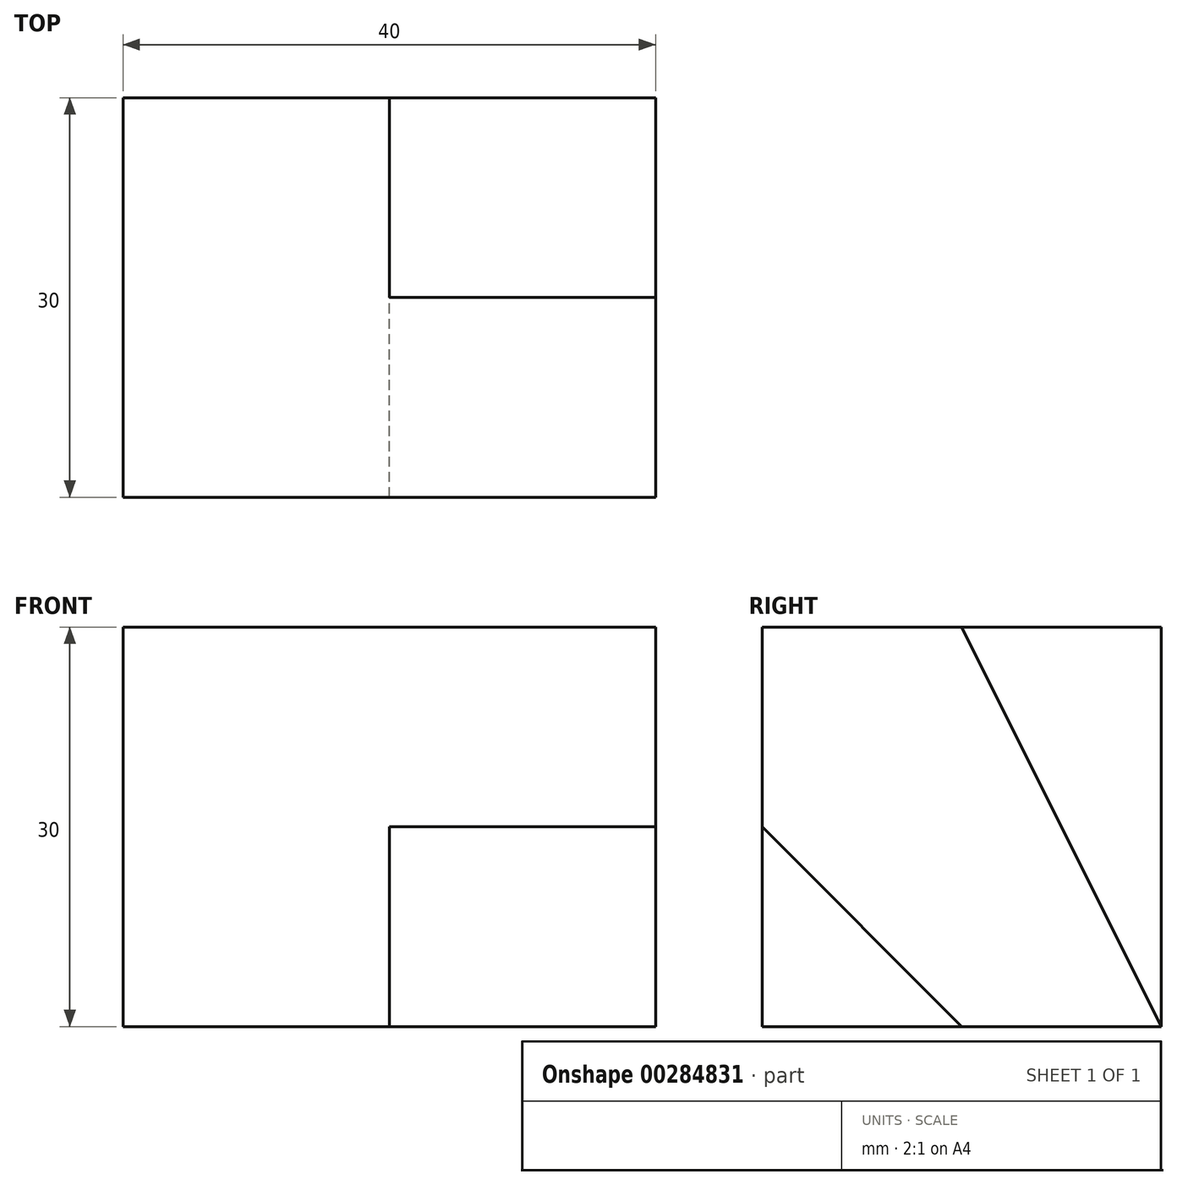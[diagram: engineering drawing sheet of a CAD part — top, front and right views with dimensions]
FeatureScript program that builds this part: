
annotation { "Feature Type Name" : "Feature", "Feature Type Description" : "" }
export const myFeature = defineFeature(function(context is Context, id is Id, definition is map)
    precondition{}
    {
        {
            var Q0;
            Q0=qCreatedBy(makeId("Right.planeOp"),FACE);
            var sketch = newSketch(context, id + "F0", { "sketchPlane" : qUnion([Q0])});
            skLineSegment(sketch, "E0.bottom", {"start": v(0, 0) * mm, "end": v(30, 0) * mm});
            skLineSegment(sketch, "E0.top", {"start": v(0, 30) * mm, "end": v(30, 30) * mm});
            skLineSegment(sketch, "E0.left", {"start": v(0, 0) * mm, "end": v(0, 30) * mm});
            skLineSegment(sketch, "E0.right", {"start": v(30, 0) * mm, "end": v(30, 30) * mm});
            skLineSegment(sketch, "E1", {"start": v(0, 15) * mm, "end": v(30, 15) * mm});
            skLineSegment(sketch, "E2", {"start": v(15, 30) * mm, "end": v(15, 0) * mm});
            skSolve(sketch);
        }
        {
            var Q0;
            Q0=qSketchRegion(id+"F0",true);
            extrude(context, id + "F1", {"entities" : qUnion([Q0]), "depth" : 20 * mm});
        }
        {
            var Q0;
            {var subQ0=sQuery(id+"F0.wireOp",EDGE,"E0.right");var subQ1=sQuery(id+"F0.wireOp",EDGE,"E0.bottom");var subQ2=makeQuery(id+"F0.imprint","INTERSECT",VERTEX,{"derivedFrom":[subQ1,subQ0]});Q0=makeQuery(id+"F0.imprint","IMPRINT",FACE,{"disambiguationData":[TD([[makeQuery(id+"F0.imprint","IMPRINT",EDGE,{"disambiguationData":[TD([[subQ2,1.0]])],"derivedFrom":subQ1}),1.0]])]});}
            var Q1;
            {var subQ0=sQuery(id+"F0.wireOp",EDGE,"E0.right");var subQ1=sQuery(id+"F0.wireOp",EDGE,"E0.top");var subQ2=makeQuery(id+"F0.imprint","INTERSECT",VERTEX,{"derivedFrom":[subQ1,subQ0]});Q1=makeQuery(id+"F0.imprint","IMPRINT",FACE,{"disambiguationData":[TD([[makeQuery(id+"F0.imprint","IMPRINT",EDGE,{"disambiguationData":[TD([[subQ2,1.0]])],"derivedFrom":subQ1}),-1.0]])]});}
            var Q2;
            {var subQ0=sQuery(id+"F0.wireOp",EDGE,"E0.left");var subQ1=sQuery(id+"F0.wireOp",EDGE,"E0.top");var subQ2=makeQuery(id+"F0.imprint","INTERSECT",VERTEX,{"derivedFrom":[subQ1,subQ0]});Q2=makeQuery(id+"F0.imprint","IMPRINT",FACE,{"disambiguationData":[TD([[makeQuery(id+"F0.imprint","IMPRINT",EDGE,{"disambiguationData":[TD([[subQ2,-1.0]])],"derivedFrom":subQ1}),-1.0]])]});}
            extrude(context, id + "F2", {"entities" : qUnion([Q0, Q1, Q2]), "operationType" : NewBodyOperationType.ADD, "depth" : 40 * mm});
        }
        {
            var Q0;
            Q0=makeQuery(id+"F2.opExtrude","CAP_FACE",FACE,{"disambiguationData":[OSD([sQuery(id+"F0.wireOp",EDGE,"E0.bottom"),sQuery(id+"F0.wireOp",EDGE,"E0.top"),sQuery(id+"F0.wireOp",EDGE,"E0.left"),sQuery(id+"F0.wireOp",EDGE,"E0.right"),sQuery(id+"F0.wireOp",EDGE,"E1"),sQuery(id+"F0.wireOp",EDGE,"E2")])],"isStart":false});
            var sketch = newSketch(context, id + "F3", { "sketchPlane" : qUnion([Q0])});
            skLineSegment(sketch, "E3", {"start": v(15, 30) * mm, "end": v(30, 0) * mm});
            skSolve(sketch);
        }
        {
            var Q0;
            Q0=qSketchRegion(id+"F3",true);
            var Q1;
            {var subQ0=sQuery(id+"F3.wireOp",EDGE,"E3");Q1=makeQuery(id+"F3.imprint","IMPRINT",FACE,{"disambiguationData":[TD([[makeQuery(id+"F3.imprint","IMPRINT",EDGE,{"derivedFrom":subQ0}),1.0]])]});}
            extrude(context, id + "F4", {"entities" : qUnion([Q0, Q1]), "operationType" : NewBodyOperationType.REMOVE, "oppositeDirection" : true, "depth" : 20 * mm});
        }
        {
            var Q0;
            Q0=makeQuery(id+"F1.opExtrude","CAP_FACE",FACE,{"disambiguationData":[OSD([sQuery(id+"F0.wireOp",EDGE,"E0.bottom"),sQuery(id+"F0.wireOp",EDGE,"E0.top"),sQuery(id+"F0.wireOp",EDGE,"E0.left"),sQuery(id+"F0.wireOp",EDGE,"E0.right")])],"isStart":false});
            var sketch = newSketch(context, id + "F5", { "sketchPlane" : qUnion([Q0])});
            skLineSegment(sketch, "E4", {"start": v(0, 15) * mm, "end": v(15, 0) * mm});
            skSolve(sketch);
        }
        {
            var Q0;
            Q0 = qSketchRegion(id + "F5", true);
            var Q1;
            Q1=makeQuery(id+"F5.imprint","IMPRINT",FACE,{"disambiguationData":[TD([[makeQuery(id+"F5.imprint","IMPRINT",EDGE,{"derivedFrom":sQuery(id+"F5.wireOp",EDGE,"E4")}),1.0]])]});
            extrude(context, id + "F6", {"entities" : qUnion([Q0, Q1]), "operationType" : NewBodyOperationType.ADD, "depth" : 20 * mm});
        }
    });
